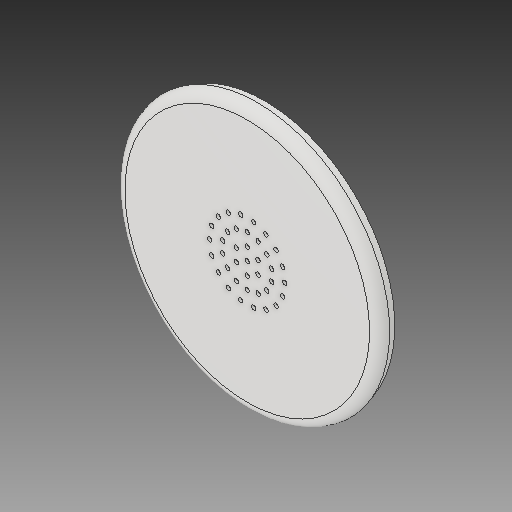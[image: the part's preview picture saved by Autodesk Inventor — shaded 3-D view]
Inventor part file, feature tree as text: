
AUTODESK INVENTOR PART (.ipt)
format: ipt  version: 2017 (Build 210142000, 142)  size: 209,408 bytes
history: native  units: mm
features: sketch x4, extrude x3, fillet x2, hole x1
ambient origin geometry x8: Origin, YZ Plane, XZ Plane, XY Plane, X Axis, Y Axis, Z Axis, Center Point
bodies: Solid1 (feature_tree)
feature tree (10):
  extrude  "Extrusion1"  Depth=7.0mm TaperAngle=0.0deg
  fillet  "Fillet1"  Radius=4.0mm
  extrude  "Extrusion2"  Depth=3.0mm TaperAngle=0.0deg
  extrude  "Extrusion3"  Depth=6.0mm
  hole  "Hole1"  [1 undecoded]
  fillet  "Fillet2"  Radius=20.0mm
  sketch  "Sketch1"  dims[d0=105.5mm d1=7.0mm d2=0.0mm d3=4.0mm]
  sketch  "Sketch2"  dims[d4=103.6mm d5=3.0mm d6=0.0mm]
  sketch  "Sketch3"  dims[d7=6.0mm d8=0.0mm d44=30.0mm]
  sketch  "Sketch6"  dims[d45=2.0mm d46=180.0mm d48=360.0deg d50=20.0mm d51=2.0mm d52=140.0mm d54=360.0deg d56=10.0mm d57=2.0mm d58=60.0mm d60=360.0deg d62=1.778mm d63=5.984mm d64=3.023mm d65=2.0mm d66=14.3117mm d67=10.688mm d68=0.0mm d69=0.0mm d70=2.0mm]
note: 1 required parameter value undecoded (feature->parameter linkage not recoverable at this tier; creation-order binding heuristic only, values carry confidence <= 0.55)
